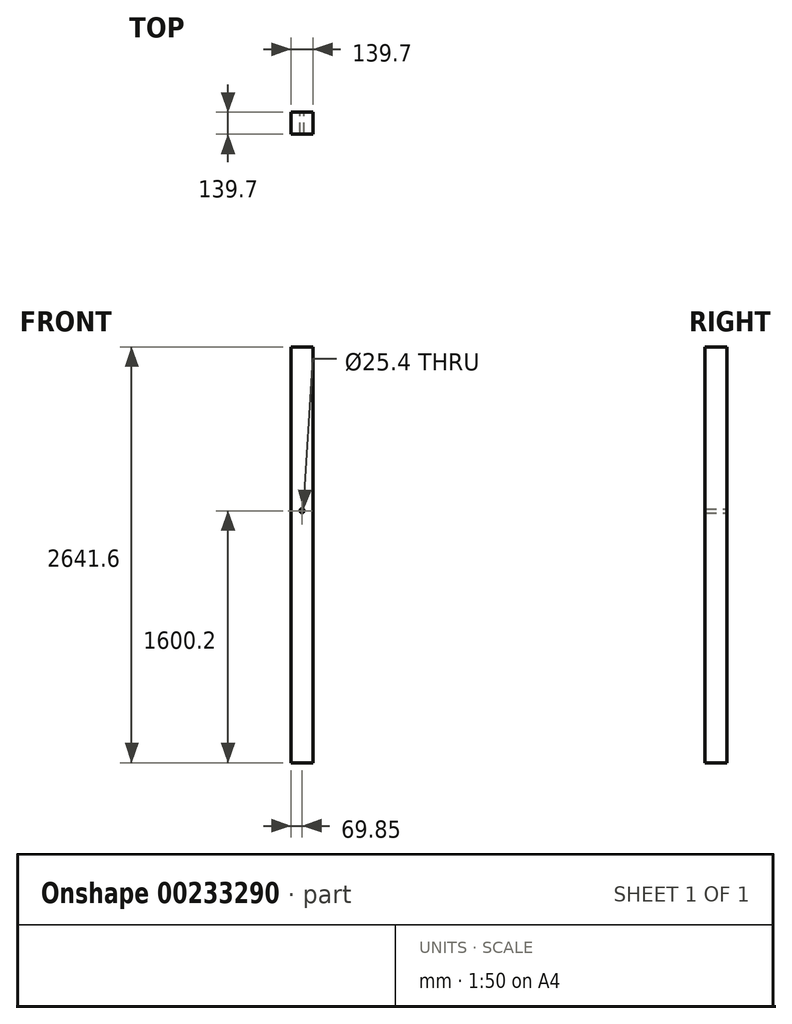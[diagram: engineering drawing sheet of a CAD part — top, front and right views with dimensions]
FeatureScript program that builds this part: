
annotation { "Feature Type Name" : "Feature", "Feature Type Description" : "" }
export const myFeature = defineFeature(function(context is Context, id is Id, definition is map)
    precondition{}
    {
        {
            var Q0;
            Q0=qCreatedBy(makeId("Front.planeOp"),FACE);
            var sketch = newSketch(context, id + "F0", { "sketchPlane" : qUnion([Q0])});
            skLineSegment(sketch, "E0.bottom", {"start": v(-69.85, 2530.48) * mm, "end": v(69.85, 2530.48) * mm});
            skLineSegment(sketch, "E0.top", {"start": v(-69.85, -111.12) * mm, "end": v(69.85, -111.12) * mm});
            skLineSegment(sketch, "E0.left", {"start": v(-69.85, 2530.48) * mm, "end": v(-69.85, -111.12) * mm});
            skLineSegment(sketch, "E0.right", {"start": v(69.85, 2530.48) * mm, "end": v(69.85, -111.12) * mm});
            skCircle(sketch, "E1", {"center": v(0, 1489.08) * mm, "radius": 12.7 * mm});
            skSolve(sketch);
        }
        {
            var Q0;
            Q0=makeQuery(id+"F0.imprint","IMPRINT",FACE,{"disambiguationData":[TD([[makeQuery(id+"F0.imprint","IMPRINT",EDGE,{"derivedFrom":sQuery(id+"F0.wireOp",EDGE,"E0.bottom")}),-1.0]])]});
            extrude(context, id + "F1", {"entities" : qUnion([Q0]), "depth" : 139.7 * mm});
        }
    });
